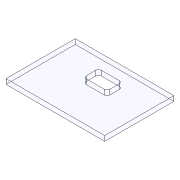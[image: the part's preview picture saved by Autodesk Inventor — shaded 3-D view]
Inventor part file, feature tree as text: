
AUTODESK INVENTOR PART (.ipt)
format: ipt  version: 2018.3 (Build 223284000, 284)  size: 100,864 bytes
history: native  units: in
note: dims shown in document units (in); Inventor stores cm internally (conversion verified against a paired STEP export)
features: extrude x2, sketch x2, fillet x1
ambient origin geometry x8: Origin, YZ Plane, XZ Plane, XY Plane, X Axis, Y Axis, Z Axis, Center Point
bodies: Solid1 (feature_tree)
feature tree (5):
  extrude  "Extrusion1"  Depth=2.315in
  extrude  "Extrusion2"  Depth=0.35in
  fillet  "Fillet1"  Radius=0.118in
  sketch  "Sketch1"  dims[d0=1.625in d1=2.315in]
  sketch  "Sketch2"  dims[d2=0.118in d3=0.0in d7=0.35in d9=0.118in d10=0.0in d11=0.0625in d17=0.55in d22=0.275in d23=0.175in d24=1.1575in d26=1.1125in]
